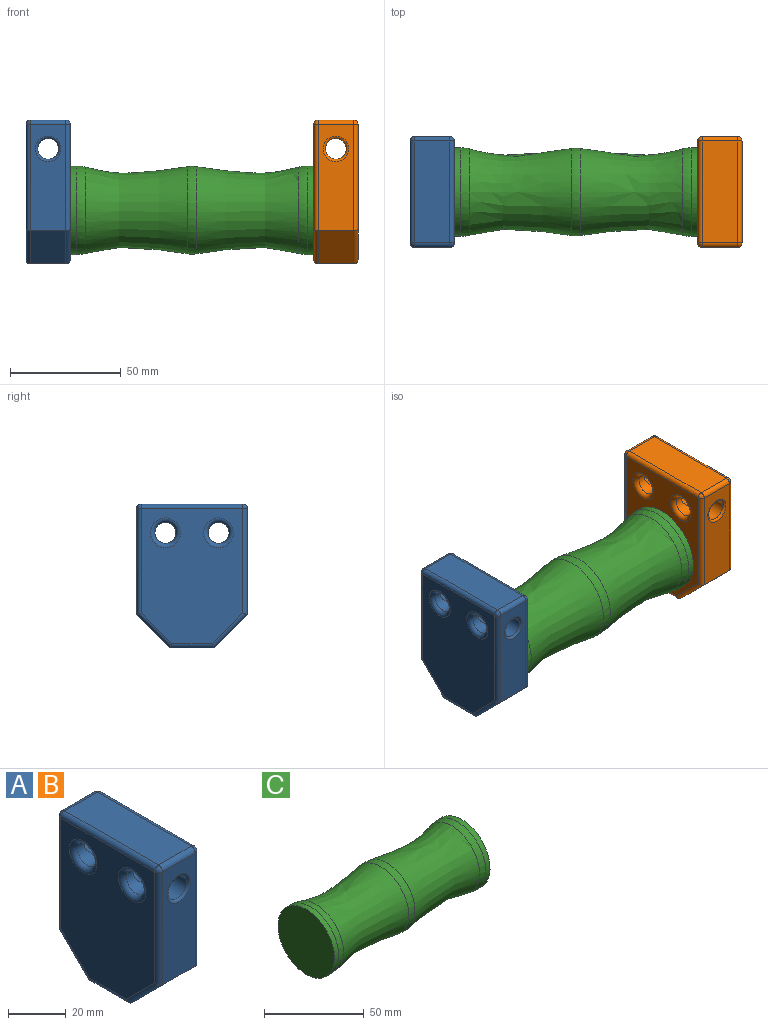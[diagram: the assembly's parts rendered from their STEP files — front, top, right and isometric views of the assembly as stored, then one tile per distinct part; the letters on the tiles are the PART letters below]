
ASSEMBLY  parts=3 mates=2
PART A: 39 faces, bbox 20x50x65 mm
  f0: cylinder r=4.75mm len=9.5mm, axis (-1,0,0), area 148.5mm2, adj f10,f11,f36
  f1: cylinder r=4.75mm len=9.5mm, axis (-1,0,0), area 148.5mm2, adj f11,f12,f33
  f2: plane 20x16mm, normal (0,0,-1), area 320mm2, adj f13,f14,f16,f31
  f3: plane 48x16mm, normal (0,1,0), area 664.1mm2, adj f14,f17,f22,f27,f37
  f4: plane 46x16mm, normal (0,0,1), area 736mm2, adj f21,f22,f25,f26
  f5: cylinder r=4.75mm len=9.5mm, axis (-1,0,0), area 148.5mm2, adj f10,f11,f34
  f6: cylinder r=4.75mm len=9.5mm, axis (-1,0,0), area 148.5mm2, adj f11,f12,f35
  f7: plane 48x16mm, normal (0,-1,0), area 664.1mm2, adj f13,f20,f25,f30,f38
  f8: plane 61x46mm, normal (1,0,0), area 2328.5mm2, adj f26,f27,f29,f30,f31,f32,f35,f36
  f9: plane 61x46mm, normal (-1,0,0), area 2328.5mm2, adj f15,f16,f17,f18,f20,f21,f33,f34
  f10: cylinder r=4.75mm len=12mm, axis (0,-1,0), area 267.9mm2, adj f0,f5,f38
  f11: cylinder r=4.75mm len=24mm, axis (0,-1,0), area 535.8mm2, adj f0,f1,f5,f6
  f12: cylinder r=4.75mm len=12mm, axis (0,-1,0), area 267.9mm2, adj f1,f6,f37
  f13: plane 16x15mm, normal (0,-0.71,-0.71), area 339.4mm2, adj f2,f7,f18,f32
  f14: plane 16x15mm, normal (0,0.71,-0.71), area 339.4mm2, adj f2,f3,f15,f29
  f15: cylinder r=2mm len=16.41mm, axis (0,0.71,0.71), area 64.8mm2, adj f9,f14,f16,f17
  f16: cylinder r=2mm len=20mm, axis (0,1,0), area 60.9mm2, adj f2,f9,f15,f18
  f17: cylinder r=2mm len=48mm, axis (0,0,1), area 149.9mm2, adj f3,f9,f15,f19
  f18: cylinder r=2mm len=16.41mm, axis (0,-0.71,0.71), area 64.8mm2, adj f9,f13,f16,f20
  f19: sphere r=2mm, area 6.3mm2, adj f17,f21,f22
  f20: cylinder r=2mm len=48mm, axis (0,0,-1), area 149.9mm2, adj f7,f9,f18,f23
  f21: cylinder r=2mm len=46mm, axis (0,-1,0), area 144.5mm2, adj f4,f9,f19,f23
  f22: cylinder r=2mm len=16mm, axis (-1,0,0), area 50.3mm2, adj f3,f4,f19,f24
  f23: sphere r=2mm, area 6.3mm2, adj f20,f21,f25
  f24: sphere r=2mm, area 6.3mm2, adj f22,f26,f27
  f25: cylinder r=2mm len=16mm, axis (1,0,0), area 50.3mm2, adj f4,f7,f23,f28
  f26: cylinder r=2mm len=46mm, axis (0,1,0), area 144.5mm2, adj f4,f8,f24,f28
  f27: cylinder r=2mm len=48mm, axis (0,0,-1), area 149.9mm2, adj f3,f8,f24,f29
  f28: sphere r=2mm, area 6.3mm2, adj f25,f26,f30
  f29: cylinder r=2mm len=16.41mm, axis (0,0.71,0.71), area 64.8mm2, adj f8,f14,f27,f31
  f30: cylinder r=2mm len=48mm, axis (0,0,1), area 149.9mm2, adj f7,f8,f28,f32
  f31: cylinder r=2mm len=20mm, axis (0,-1,0), area 60.9mm2, adj f2,f8,f29,f32
  f32: cylinder r=2mm len=16.41mm, axis (0,-0.71,0.71), area 64.8mm2, adj f8,f13,f30,f31
  f33: torus R=6.75mm, axis (1,0,0), area 108.1mm2, adj f1,f9
  f34: torus R=6.75mm, axis (1,0,0), area 108.1mm2, adj f5,f9
  f35: torus R=6.75mm, axis (1,0,0), area 108.1mm2, adj f6,f8
  f36: torus R=6.75mm, axis (1,0,0), area 108.1mm2, adj f0,f8
  f37: torus R=5.75mm, axis (0,-1,0), area 50.5mm2, adj f3,f12
  f38: torus R=5.75mm, axis (0,-1,0), area 50.5mm2, adj f7,f10
PART B: same geometry as A
PART C: 9 faces, bbox 110x40x40 mm
  f0: plane 40x40mm, normal (1,0,0), area 1256.6mm2, adj f1
  f1: cylinder r=20mm len=40mm, axis (-1,0,0), area 377.4mm2, adj f0,f2
  f2: torus R=5mm, axis (1,0,0), area 489.9mm2, adj f1,f3
  f3: revolved ~45.89x39.33mm, area 5188.9mm2, adj f2,f4
  f4: torus R=4.83mm, axis (1,0,0), area 554.6mm2, adj f3
  f5: cylinder r=20mm len=40mm, axis (-1,0,0), area 377.4mm2, adj f6,f7
  f6: plane 40x40mm, normal (-1,0,0), area 1256.6mm2, adj f5
  f7: torus R=5mm, axis (1,0,0), area 489.9mm2, adj f5
  f8: revolved ~45.89x39.33mm, area 10377.8mm2
PLACE A t=(-65,0,8.27)mm
PLACE B t=(65,0,8.27)mm
PLACE C at identity
MATE fastened B.f9 <-> C.f1  axis (-1,0,0) through (55,0,0)mm
MATE fastened A.f8 <-> C.f1  axis (1,0,0) through (-55,0,0)mm
